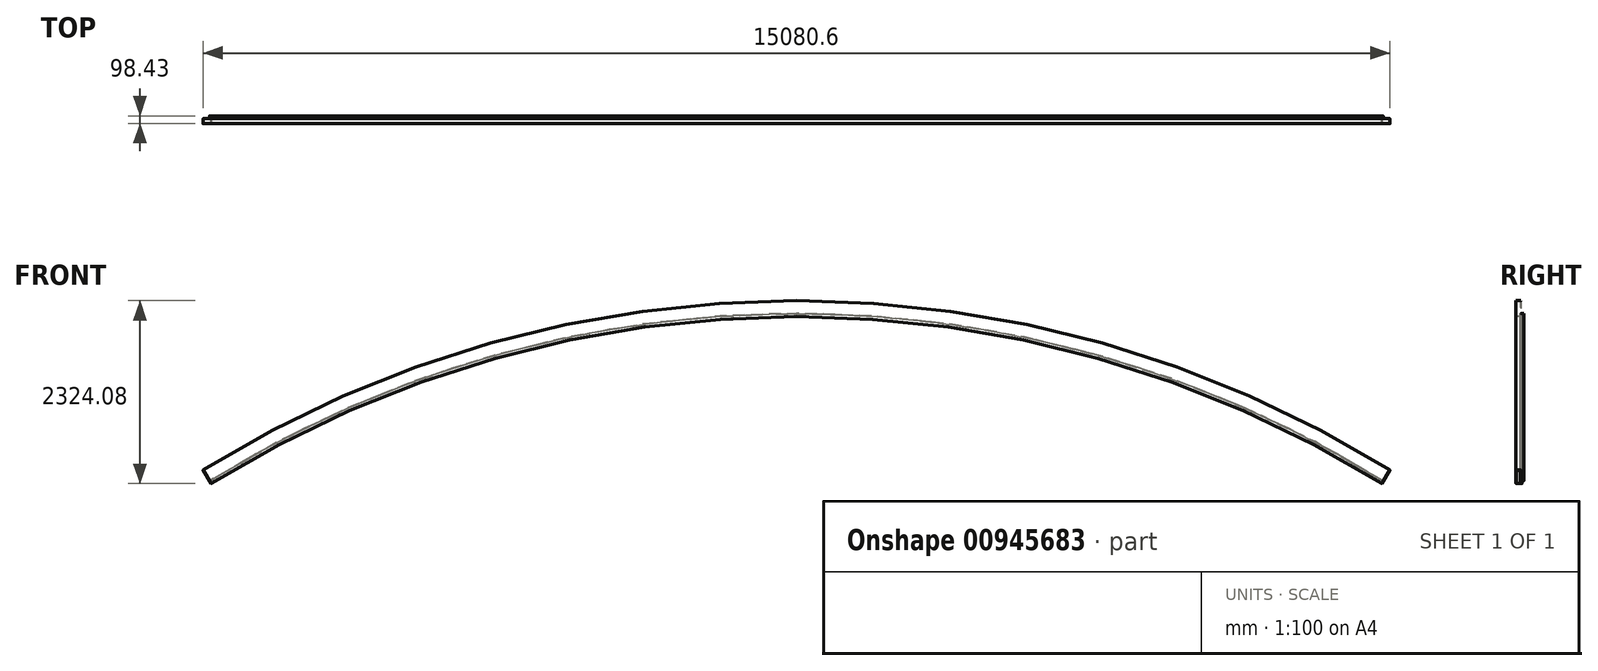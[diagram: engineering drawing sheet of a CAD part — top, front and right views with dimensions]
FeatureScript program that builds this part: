
annotation { "Feature Type Name" : "Feature", "Feature Type Description" : "" }
export const myFeature = defineFeature(function(context is Context, id is Id, definition is map)
    precondition{}
    {
        {
            var Q0;
            Q0=qCreatedBy(makeId("Right.planeOp"),FACE);
            var sketch = newSketch(context, id + "F0", { "sketchPlane" : qUnion([Q0])});
            skLineSegment(sketch, "E0", {"start": v(-44.46, 0) * mm, "end": v(31.23, 0) * mm});
            skLineSegment(sketch, "E1", {"start": v(31.48, 0.25) * mm, "end": v(31.48, 37.85) * mm});
            skLineSegment(sketch, "E2", {"start": v(31.74, 38.1) * mm, "end": v(46.75, 38.1) * mm});
            skLineSegment(sketch, "E3", {"start": v(53.7, 38.35) * mm, "end": v(53.7, 41.02) * mm});
            skLineSegment(sketch, "E4", {"start": v(53.45, 41.28) * mm, "end": v(21.2, 41.28) * mm});
            skLineSegment(sketch, "E5", {"start": v(9.26, 41.02) * mm, "end": v(9.26, 37.73) * mm});
            skLineSegment(sketch, "E6", {"start": v(15.72, 38.1) * mm, "end": v(24.78, 38.1) * mm});
            skLineSegment(sketch, "E7", {"start": v(28.3, 37.85) * mm, "end": v(28.3, 3.43) * mm});
            skLineSegment(sketch, "E8", {"start": v(28.05, 3.18) * mm, "end": v(-41.29, 3.17) * mm});
            skLineSegment(sketch, "E9", {"start": v(-41.54, 3.43) * mm, "end": v(-41.54, 199.77) * mm});
            skLineSegment(sketch, "E10", {"start": v(-41.29, 200.03) * mm, "end": v(18.53, 200.03) * mm});
            skLineSegment(sketch, "E11", {"start": v(18.78, 200.28) * mm, "end": v(18.78, 202.95) * mm});
            skLineSegment(sketch, "E12", {"start": v(18.53, 203.2) * mm, "end": v(-44.46, 203.2) * mm});
            skLineSegment(sketch, "E13", {"start": v(-44.72, 202.95) * mm, "end": v(-44.72, 0.25) * mm});
            skArc(sketch, "E14", {"start": v(20.21, 41.12) * mm, "mid": v(20.59, 40.87) * mm, "end": v(20.96, 41.12) * mm});
            skArc(sketch, "E15", {"start": v(47.73, 38.26) * mm, "mid": v(47.36, 38.5) * mm, "end": v(46.98, 38.26) * mm});
            skArc(sketch, "E16", {"start": v(24.99, 37.99) * mm, "mid": v(25.16, 37.9) * mm, "end": v(25.33, 37.99) * mm});
            skArc(sketch, "E17", {"start": v(9.35, 37.53) * mm, "mid": v(12.54, 36.54) * mm, "end": v(15.53, 38.02) * mm});
            skLineSegment(sketch, "E18.trimOffspring", {"start": v(19.98, 41.28) * mm, "end": v(9.51, 41.28) * mm});
            skLineSegment(sketch, "E19.trimOffspring", {"start": v(25.54, 38.1) * mm, "end": v(28.05, 38.1) * mm});
            skLineSegment(sketch, "E20.trimOffspring", {"start": v(47.97, 38.1) * mm, "end": v(53.45, 38.1) * mm});
            skPoint(sketch, "E21.visualSharp", {"position": v(53.7, 41.28) * mm});
            skArc(sketch, "E21.filletArc", {"start": v(53.7, 41.02) * mm, "mid": v(53.63, 41.2) * mm, "end": v(53.45, 41.28) * mm});
            skPoint(sketch, "E22.visualSharp", {"position": v(53.7, 38.1) * mm});
            skArc(sketch, "E22.filletArc", {"start": v(53.45, 38.1) * mm, "mid": v(53.63, 38.17) * mm, "end": v(53.7, 38.35) * mm});
            skPoint(sketch, "E23.visualSharp", {"position": v(31.48, 38.1) * mm});
            skArc(sketch, "E23.filletArc", {"start": v(31.74, 38.1) * mm, "mid": v(31.56, 38.03) * mm, "end": v(31.48, 37.85) * mm});
            skPoint(sketch, "E24.visualSharp", {"position": v(28.3, 38.1) * mm});
            skArc(sketch, "E24.filletArc", {"start": v(28.3, 37.85) * mm, "mid": v(28.23, 38.03) * mm, "end": v(28.05, 38.1) * mm});
            skPoint(sketch, "E25.visualSharp", {"position": v(46.95, 38.1) * mm});
            skArc(sketch, "E25.filletArc", {"start": v(46.75, 38.1) * mm, "mid": v(46.89, 38.14) * mm, "end": v(46.98, 38.26) * mm});
            skPoint(sketch, "E26.visualSharp", {"position": v(47.76, 38.1) * mm});
            skArc(sketch, "E26.filletArc", {"start": v(47.73, 38.26) * mm, "mid": v(47.83, 38.14) * mm, "end": v(47.97, 38.1) * mm});
            skPoint(sketch, "E27.visualSharp", {"position": v(21, 41.28) * mm});
            skArc(sketch, "E27.filletArc", {"start": v(21.2, 41.28) * mm, "mid": v(21.05, 41.23) * mm, "end": v(20.96, 41.12) * mm});
            skPoint(sketch, "E28.visualSharp", {"position": v(20.18, 41.28) * mm});
            skArc(sketch, "E28.filletArc", {"start": v(20.21, 41.12) * mm, "mid": v(20.12, 41.23) * mm, "end": v(19.98, 41.28) * mm});
            skPoint(sketch, "E29.visualSharp", {"position": v(25.36, 38.1) * mm});
            skArc(sketch, "E29.filletArc", {"start": v(25.54, 38.1) * mm, "mid": v(25.42, 38.07) * mm, "end": v(25.33, 37.99) * mm});
            skPoint(sketch, "E30.visualSharp", {"position": v(24.95, 38.1) * mm});
            skArc(sketch, "E30.filletArc", {"start": v(24.99, 37.99) * mm, "mid": v(24.9, 38.07) * mm, "end": v(24.78, 38.1) * mm});
            skPoint(sketch, "E31.visualSharp", {"position": v(15.6, 38.1) * mm});
            skArc(sketch, "E31.filletArc", {"start": v(15.72, 38.1) * mm, "mid": v(15.62, 38.08) * mm, "end": v(15.53, 38.02) * mm});
            skPoint(sketch, "E32.visualSharp", {"position": v(9.26, 37.61) * mm});
            skArc(sketch, "E32.filletArc", {"start": v(9.26, 37.73) * mm, "mid": v(9.28, 37.62) * mm, "end": v(9.35, 37.53) * mm});
            skPoint(sketch, "E33.visualSharp", {"position": v(9.26, 41.28) * mm});
            skArc(sketch, "E33.filletArc", {"start": v(9.51, 41.28) * mm, "mid": v(9.33, 41.2) * mm, "end": v(9.26, 41.02) * mm});
            skPoint(sketch, "E34.visualSharp", {"position": v(28.3, 3.18) * mm});
            skArc(sketch, "E34.filletArc", {"start": v(28.05, 3.18) * mm, "mid": v(28.23, 3.25) * mm, "end": v(28.3, 3.43) * mm});
            skPoint(sketch, "E35.visualSharp", {"position": v(31.48, 0) * mm});
            skArc(sketch, "E35.filletArc", {"start": v(31.23, 0) * mm, "mid": v(31.4, 0.07) * mm, "end": v(31.48, 0.25) * mm});
            skPoint(sketch, "E36.visualSharp", {"position": v(-44.72, 0) * mm});
            skArc(sketch, "E36.filletArc", {"start": v(-44.72, 0.25) * mm, "mid": v(-44.64, 0.07) * mm, "end": v(-44.46, 0) * mm});
            skPoint(sketch, "E37.visualSharp", {"position": v(-41.54, 3.17) * mm});
            skArc(sketch, "E37.filletArc", {"start": v(-41.54, 3.43) * mm, "mid": v(-41.47, 3.25) * mm, "end": v(-41.29, 3.17) * mm});
            skPoint(sketch, "E38.visualSharp", {"position": v(-44.72, 203.2) * mm});
            skArc(sketch, "E38.filletArc", {"start": v(-44.46, 203.2) * mm, "mid": v(-44.64, 203.13) * mm, "end": v(-44.72, 202.95) * mm});
            skPoint(sketch, "E39.visualSharp", {"position": v(-41.54, 200.03) * mm});
            skArc(sketch, "E39.filletArc", {"start": v(-41.29, 200.03) * mm, "mid": v(-41.47, 199.95) * mm, "end": v(-41.54, 199.77) * mm});
            skPoint(sketch, "E40.visualSharp", {"position": v(18.78, 203.2) * mm});
            skArc(sketch, "E40.filletArc", {"start": v(18.78, 202.95) * mm, "mid": v(18.7, 203.13) * mm, "end": v(18.53, 203.2) * mm});
            skPoint(sketch, "E41.visualSharp", {"position": v(18.78, 200.03) * mm});
            skArc(sketch, "E41.filletArc", {"start": v(18.53, 200.03) * mm, "mid": v(18.7, 200.1) * mm, "end": v(18.78, 200.28) * mm});
            skSolve(sketch);
        }
        {
            var Q0;
            Q0=qCreatedBy(makeId("Right.planeOp"),FACE);
            var sketch = newSketch(context, id + "F1", { "sketchPlane" : qUnion([Q0])});
            skLineSegment(sketch, "E42", {"start": v(-12421.45, -14085.89) * mm, "end": v(12443.27, -14085.89) * mm, "construction": true});
            skSolve(sketch);
        }
        {
            var Q0;
            Q0=qSketchRegion(id+"F0",true);
            var Q1;
            Q1=sQuery(id+"F1.wireOp",EDGE,"E42");
            revolve(context, id + "F2", {"entities" : qUnion([Q0]), "axis" : qUnion([Q1]), "revolveType" : RevolveType.SYMMETRIC, "angle" : 63.7 * degree, "surfaceOperationType" : NewSurfaceOperationType.NEW});
        }
    });
